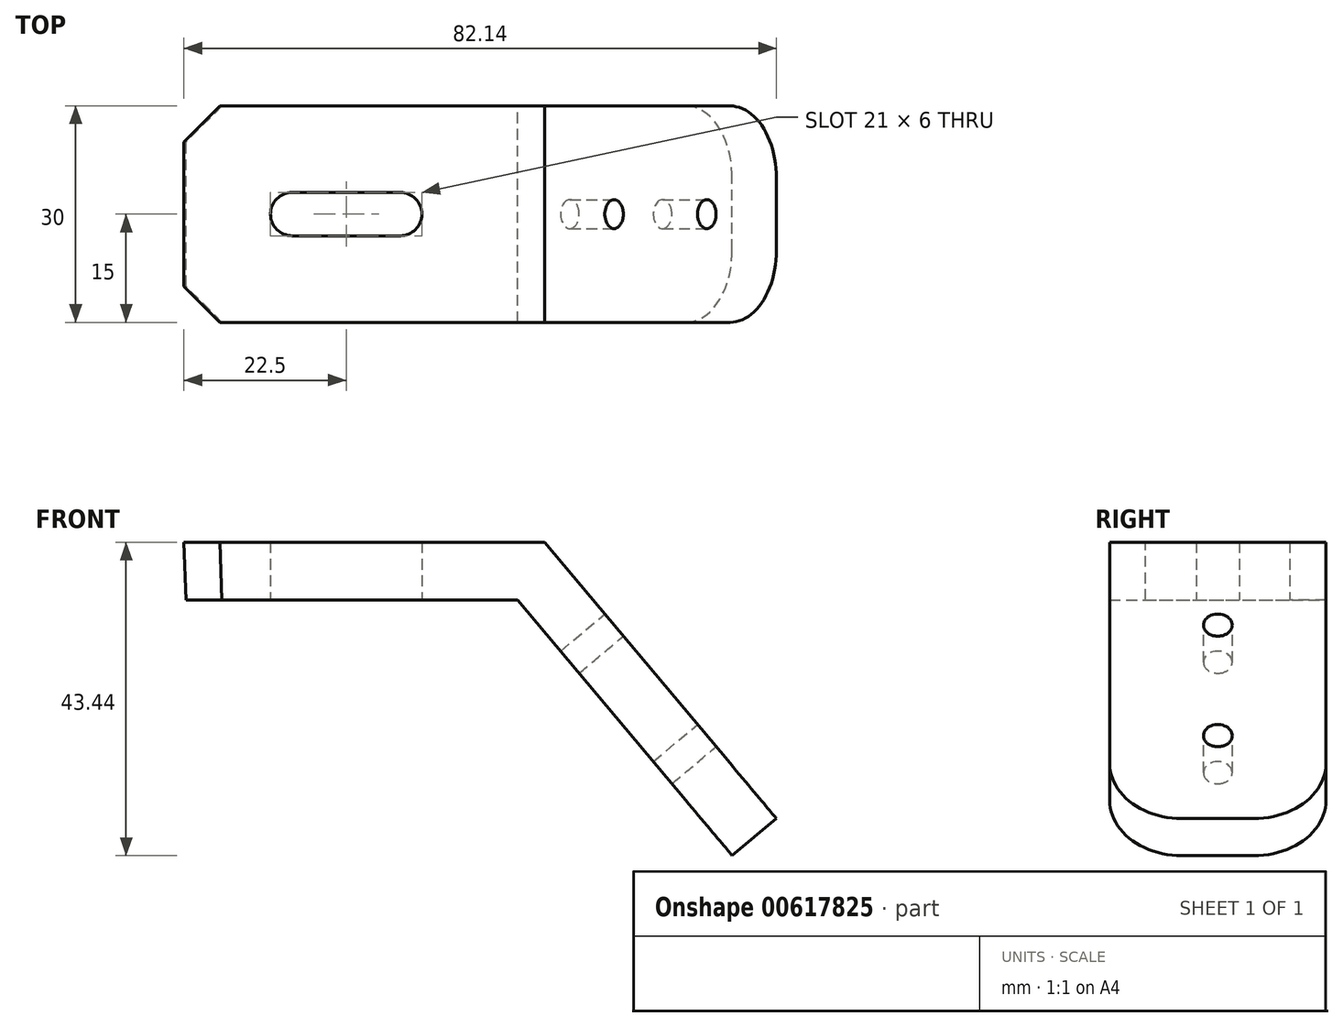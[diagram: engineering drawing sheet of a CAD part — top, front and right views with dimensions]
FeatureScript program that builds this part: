
annotation { "Feature Type Name" : "Feature", "Feature Type Description" : "" }
export const myFeature = defineFeature(function(context is Context, id is Id, definition is map)
    precondition{}
    {
        {
            var Q0;
            Q0=qCreatedBy(makeId("Front.planeOp"),FACE);
            var sketch = newSketch(context, id + "F0", { "sketchPlane" : qUnion([Q0])});
            skLineSegment(sketch, "E0", {"start": v(46, 0) * mm, "end": v(75.74, -35.44) * mm});
            skLineSegment(sketch, "E1", {"start": v(0, 0) * mm, "end": v(46, 0) * mm});
            skLineSegment(sketch, "E2.0", {"start": v(49.73, 8) * mm, "end": v(81.87, -30.3) * mm});
            skLineSegment(sketch, "E2.1", {"start": v(-0.27, 8) * mm, "end": v(49.73, 8) * mm});
            skLineSegment(sketch, "E3", {"start": v(-0.27, 8) * mm, "end": v(0, 0) * mm});
            skLineSegment(sketch, "E4", {"start": v(75.74, -35.44) * mm, "end": v(81.87, -30.3) * mm});
            skSolve(sketch);
        }
        {
            var Q0;
            Q0 = qSketchRegion(id + "F0", true);
            extrude(context, id + "F1", {"entities" : qUnion([Q0]), "endBound" : BoundingType.SYMMETRIC, "depth" : 30 * mm, "offsetDistance" : 25 * mm});
        }
        {
            var Q0;
            Q0=qCreatedBy(makeId("Top.planeOp"),FACE);
            var sketch = newSketch(context, id + "F2", { "sketchPlane" : qUnion([Q0])});
            skLineSegment(sketch, "E5", {"start": v(14.73, 0) * mm, "end": v(29.73, 0) * mm});
            skArc(sketch, "E6.0.startCap", {"start": v(14.73, -3) * mm, "mid": v(11.73, 0) * mm, "end": v(14.73, 3) * mm});
            skArc(sketch, "E6.0.endCap", {"start": v(29.73, 3) * mm, "mid": v(32.73, 0) * mm, "end": v(29.73, -3) * mm});
            skLineSegment(sketch, "E6.0.left", {"start": v(14.73, 3) * mm, "end": v(29.73, 3) * mm});
            skLineSegment(sketch, "E6.0.right", {"start": v(14.73, -3) * mm, "end": v(29.73, -3) * mm});
            skSolve(sketch);
        }
        {
            var Q0;
            Q0 = qSketchRegion(id + "F2", true);
            extrude(context, id + "F3", {"entities" : qUnion([Q0]), "operationType" : NewBodyOperationType.REMOVE, "endBound" : BoundingType.THROUGH_ALL, "depth" : 25 * mm, "offsetDistance" : 25 * mm});
        }
        {
            var Q0;
            Q0=makeQuery(id+"F1.opExtrude","SWEPT_FACE",FACE,{"disambiguationData":[OSD([sQuery(id+"F0.wireOp",EDGE,"E2.0")])]});
            var sketch = newSketch(context, id + "F4", { "sketchPlane" : qUnion([Q0])});
            skPoint(sketch, "E7", {"position": v(0, -40.84) * mm});
            skPoint(sketch, "E8", {"position": v(0, -60.84) * mm});
            skSolve(sketch);
        }
        {
            var Q0;
            Q0=sQuery(id+"F4.wireOp",VERTEX,"E7");
            var Q1;
            Q1=sQuery(id+"F4.wireOp",VERTEX,"E8");
            var Q2;
            Q2=makeQuery(id+"F1.opExtrude","SWEPT_BODY",BODY,{"disambiguationData":[OSD([sQuery(id+"F0.wireOp",EDGE,"E0"),sQuery(id+"F0.wireOp",EDGE,"E1"),sQuery(id+"F0.wireOp",EDGE,"E2.0"),sQuery(id+"F0.wireOp",EDGE,"E2.1"),sQuery(id+"F0.wireOp",EDGE,"E3"),sQuery(id+"F0.wireOp",EDGE,"E4")])]});
            hole(context, id + "F5", {"style" : HoleStyle.SIMPLE, "endStyle" : HoleEndStyle.THROUGH, "holeDiameter" : 4 * mm, "majorDiameter" : 5 * mm, "isTappedThrough" : true, "tappedDepth" : 12 * mm, "tapClearance" : 3, "locations" : qUnion([Q0, Q1]), "scope" : qUnion([Q2])});
        }
        {
            var Q0;
            Q0=makeQuery(id+"F1.opExtrude","CAP_EDGE",EDGE,{"disambiguationData":[OSD([sQuery(id+"F0.wireOp",EDGE,"E4")])],"isStart":false});
            var Q1;
            Q1=makeQuery(id+"F1.opExtrude","CAP_EDGE",EDGE,{"disambiguationData":[OSD([sQuery(id+"F0.wireOp",EDGE,"E4")])],"isStart":true});
            fillet(context, id + "F6", {"entities" : qUnion([Q0, Q1]), "radius" : 10 * mm, "tangentPropagation" : true, "allowEdgeOverflow" : false});
        }
        {
            var Q0;
            Q0=makeQuery(id+"F1.opExtrude","CAP_EDGE",EDGE,{"disambiguationData":[OSD([sQuery(id+"F0.wireOp",EDGE,"E3")])],"isStart":true});
            var Q1;
            Q1=makeQuery(id+"F1.opExtrude","CAP_EDGE",EDGE,{"disambiguationData":[OSD([sQuery(id+"F0.wireOp",EDGE,"E3")])],"isStart":false});
            chamfer(context, id + "F7", {"entities" : qUnion([Q0, Q1]), "width" : 5 * mm, "tangentPropagation" : true});
        }
    });
